# Revit family: Skid
name_source: partatom
category: Generic Models
units: mm (PartAtom-declared; Revit-internal decimal feet)

## family parameters
Always vertical = Yes
Can host rebar = No
Cut with Voids When Loaded = No
Maintain Annotation Orientation = No
Part Type = Normal
Room Calculation Point = No
Round Connector Dimension = Use Diameter
Shared = No
Work Plane-Based = No

## types (3) — shared parameters
hauteur palais = 20 mm  [stored 0.0656168 ft]
hauteur pied = 70 mm  [stored 0.229659 ft]
largeur profilé = 60 mm  [stored 0.19685 ft]
zero-valued in all types: Default Elevation

## per-type parameters (varying)
| type | URL | hauteur profilé | hauteur skid | largeur skid | longueur skid |
| 2000 x 1000 x 1500ht |  | 60 mm  [stored 0.19685 ft] | 1500 mm  [stored 4.92126 ft] | 1000 mm  [stored 3.28084 ft] | 2000 mm  [stored 6.56168 ft] |
| 1800 x 700 x 1800ht | blog.cad4cvc.ch | 60 mm  [stored 0.19685 ft] | 1800 mm  [stored 5.90551 ft] | 700 mm  [stored 2.29659 ft] | 1800 mm  [stored 5.90551 ft] |
| 2000 x 2000 x 2000ht |  | 100 mm  [stored 0.328084 ft] | 2000 mm  [stored 6.56168 ft] | 2000 mm  [stored 6.56168 ft] | 2000 mm  [stored 6.56168 ft] |

note: [stored X ft] marks values corroborated as IEEE doubles in the binary element streams (Revit-internal decimal feet)
